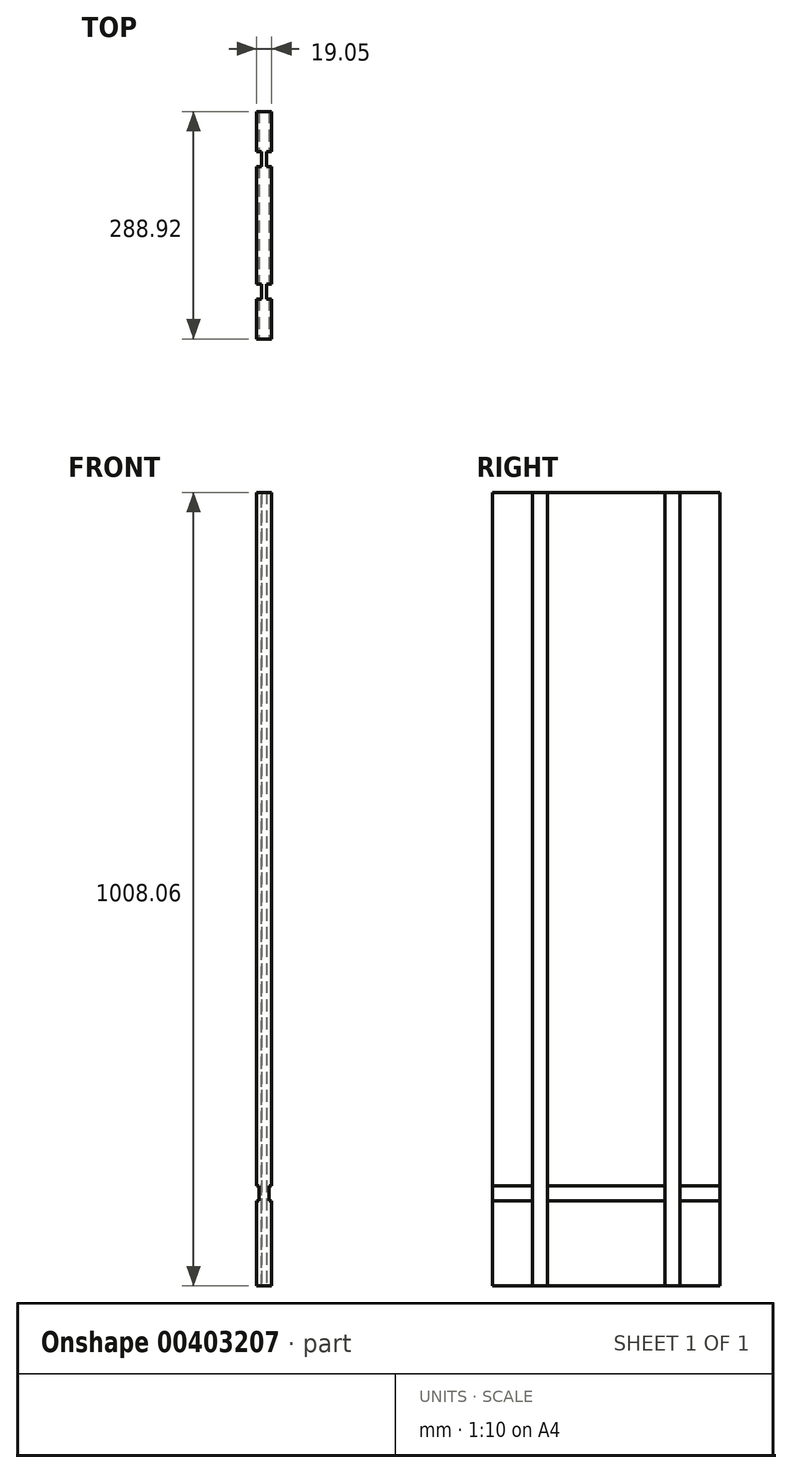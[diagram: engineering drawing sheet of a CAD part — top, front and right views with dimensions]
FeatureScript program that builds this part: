
annotation { "Feature Type Name" : "Feature", "Feature Type Description" : "" }
export const myFeature = defineFeature(function(context is Context, id is Id, definition is map)
    precondition{}
    {
        {
            var Q0;
            Q0=qCreatedBy(makeId("Right.planeOp"),FACE);
            var sketch = newSketch(context, id + "F0", { "sketchPlane" : qUnion([Q0])});
            skLineSegment(sketch, "E0.bottom", {"start": v(144.46, -504.03) * mm, "end": v(-144.46, -504.03) * mm});
            skLineSegment(sketch, "E0.top", {"start": v(144.46, 504.03) * mm, "end": v(-144.46, 504.03) * mm});
            skLineSegment(sketch, "E0.left", {"start": v(144.46, -504.03) * mm, "end": v(144.46, 504.03) * mm});
            skLineSegment(sketch, "E0.right", {"start": v(-144.46, -504.03) * mm, "end": v(-144.46, 504.03) * mm});
            skPoint(sketch, "E0.middle", {"position": v(0, 0) * mm});
            skSolve(sketch);
        }
        {
            var Q0;
            Q0=makeQuery(id+"F0.imprint","IMPRINT",FACE,{"disambiguationData":[TD([[makeQuery(id+"F0.imprint","IMPRINT",EDGE,{"derivedFrom":sQuery(id+"F0.wireOp",EDGE,"E0.bottom")}),-1.0]])]});
            extrude(context, id + "F1", {"entities" : qUnion([Q0]), "depth" : 19.05 * mm});
        }
        {
            var Q0;
            {var subQ0=sQuery(id+"F0.wireOp",EDGE,"E0.top");var subQ1=sQuery(id+"F0.wireOp",EDGE,"E0.left");var subQ2=sQuery(id+"F0.wireOp",EDGE,"E0.right");Q0=makeQuery(id+"FHFzetuikgtx7Z4_1.boolean.opBoolean","SPLIT",FACE,{"disambiguationData":[TD([makeQuery(id+"F1.opExtrude","SWEPT_FACE",FACE,{"disambiguationData":[OSD([subQ0])]})])],"derivedFrom":makeQuery(id+"F1.opExtrude","CAP_FACE",FACE,{"disambiguationData":[OSD([sQuery(id+"F0.wireOp",EDGE,"E0.bottom"),subQ0,subQ1,subQ2])],"isStart":false})});}
            var sketch = newSketch(context, id + "F2", { "sketchPlane" : qUnion([Q0])});
            skLineSegment(sketch, "E1.bottom", {"start": v(-93.66, 504.03) * mm, "end": v(-74.61, 504.03) * mm});
            skLineSegment(sketch, "E1.top", {"start": v(-93.66, -504.03) * mm, "end": v(-74.61, -504.03) * mm});
            skLineSegment(sketch, "E1.left", {"start": v(-93.66, 504.03) * mm, "end": v(-93.66, -504.03) * mm});
            skLineSegment(sketch, "E1.right", {"start": v(-74.61, 504.03) * mm, "end": v(-74.61, -504.03) * mm});
            skLineSegment(sketch, "E2", {"start": v(0, 504.03) * mm, "end": v(0, -504.03) * mm, "construction": true});
            skLineSegment(sketch, "E3.MirrorCS", {"start": v(93.66, -504.03) * mm, "end": v(74.61, -504.03) * mm});
            skLineSegment(sketch, "E4.MirrorCS", {"start": v(93.66, 504.03) * mm, "end": v(74.61, 504.03) * mm});
            skLineSegment(sketch, "E5.MirrorCS", {"start": v(74.61, 504.03) * mm, "end": v(74.61, -504.03) * mm});
            skLineSegment(sketch, "E6.MirrorCS", {"start": v(93.66, 504.03) * mm, "end": v(93.66, -504.03) * mm});
            skSolve(sketch);
        }
        {
            var Q0;
            Q0=qSketchRegion(id+"F2",true);
            extrude(context, id + "F3", {"entities" : qUnion([Q0]), "operationType" : NewBodyOperationType.REMOVE, "oppositeDirection" : true, "depth" : 6.35 * mm});
        }
        {
            var Q0;
            Q0=makeQuery(id+"F1.opExtrude","CAP_FACE",FACE,{"disambiguationData":[OSD([sQuery(id+"F0.wireOp",EDGE,"E0.bottom"),sQuery(id+"F0.wireOp",EDGE,"E0.top"),sQuery(id+"F0.wireOp",EDGE,"E0.left"),sQuery(id+"F0.wireOp",EDGE,"E0.right")])],"isStart":true});
            var sketch = newSketch(context, id + "F4", { "sketchPlane" : qUnion([Q0])});
            skLineSegment(sketch, "E7.0", {"start": v(93.66, 504.03) * mm, "end": v(93.66, -377.03) * mm});
            skLineSegment(sketch, "E8.0", {"start": v(74.61, 504.03) * mm, "end": v(74.61, -377.03) * mm});
            skLineSegment(sketch, "E9.0", {"start": v(-93.66, 504.03) * mm, "end": v(-93.66, -377.03) * mm});
            skLineSegment(sketch, "E10.0", {"start": v(-74.61, 504.03) * mm, "end": v(-74.61, -377.03) * mm});
            skLineSegment(sketch, "E11", {"start": v(-93.66, -504.03) * mm, "end": v(-74.61, -504.03) * mm});
            skLineSegment(sketch, "E12", {"start": v(74.61, -504.03) * mm, "end": v(93.66, -504.03) * mm});
            skLineSegment(sketch, "E13", {"start": v(-93.66, 504.03) * mm, "end": v(-74.61, 504.03) * mm});
            skLineSegment(sketch, "E14", {"start": v(74.61, 504.03) * mm, "end": v(93.66, 504.03) * mm});
            skLineSegment(sketch, "E15", {"start": v(-93.66, -504.03) * mm, "end": v(-93.66, -377.03) * mm});
            skLineSegment(sketch, "E16", {"start": v(-74.61, -504.03) * mm, "end": v(-74.61, -377.03) * mm});
            skLineSegment(sketch, "E17", {"start": v(74.61, -504.03) * mm, "end": v(74.61, -377.03) * mm});
            skLineSegment(sketch, "E18", {"start": v(93.66, -504.03) * mm, "end": v(93.66, -377.03) * mm});
            skSolve(sketch);
        }
        {
            var Q0;
            Q0 = qSketchRegion(id + "F4", true);
            extrude(context, id + "F5", {"entities" : qUnion([Q0]), "operationType" : NewBodyOperationType.REMOVE, "oppositeDirection" : true, "depth" : 6.35 * mm});
        }
        {
            var Q0;
            Q0=makeQuery(id+"F1.opExtrude","SWEPT_FACE",FACE,{"disambiguationData":[OSD([sQuery(id+"F0.wireOp",EDGE,"E0.right")])]});
            var sketch = newSketch(context, id + "F6", { "sketchPlane" : qUnion([Q0])});
            skLineSegment(sketch, "E19.bottom", {"start": v(0, -396.08) * mm, "end": v(3.17, -396.08) * mm});
            skLineSegment(sketch, "E19.top", {"start": v(0, -377.03) * mm, "end": v(3.17, -377.03) * mm});
            skLineSegment(sketch, "E19.left", {"start": v(0, -396.08) * mm, "end": v(0, -377.03) * mm});
            skLineSegment(sketch, "E19.right", {"start": v(3.17, -396.08) * mm, "end": v(3.17, -377.03) * mm});
            skLineSegment(sketch, "E20", {"start": v(9.53, -504.03) * mm, "end": v(9.53, 504.03) * mm, "construction": true});
            skLineSegment(sketch, "E21.MirrorCS", {"start": v(19.05, -396.08) * mm, "end": v(15.88, -396.08) * mm});
            skLineSegment(sketch, "E22.MirrorCS", {"start": v(19.05, -377.03) * mm, "end": v(15.88, -377.03) * mm});
            skLineSegment(sketch, "E23.MirrorCS", {"start": v(15.88, -396.08) * mm, "end": v(15.88, -377.03) * mm});
            skLineSegment(sketch, "E24.MirrorCS", {"start": v(19.05, -396.08) * mm, "end": v(19.05, -377.03) * mm});
            skSolve(sketch);
        }
        {
            var Q0;
            Q0 = qSketchRegion(id + "F6", true);
            extrude(context, id + "F7", {"entities" : qUnion([Q0]), "operationType" : NewBodyOperationType.REMOVE, "endBound" : BoundingType.THROUGH_ALL, "oppositeDirection" : true, "depth" : 25.4 * mm});
        }
    });
